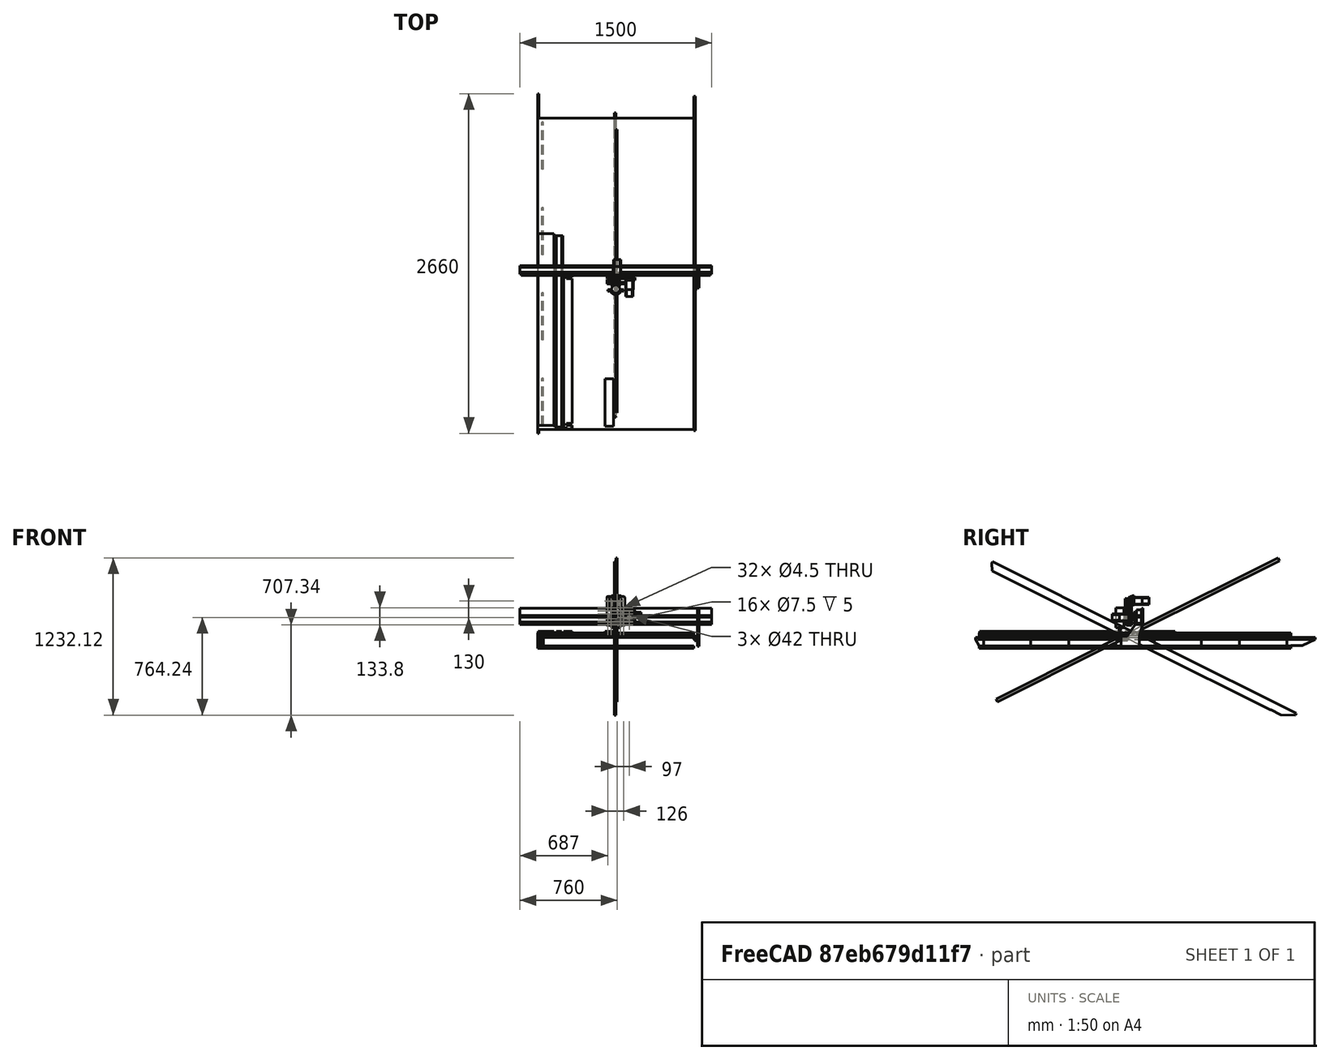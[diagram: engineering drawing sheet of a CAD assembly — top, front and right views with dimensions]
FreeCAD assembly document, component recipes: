
FREECAD ASSEMBLY — COMPONENT RECIPES ("humphrey2")

This assembly document has 11 components, labeled P0..P10 below (a component is one placed body or linked part). 10 of them carry a construction recipe — the FreeCAD feature program that regenerates the part from scratch, quoted from this document or its linked companion documents; the rest are supplied as boundary geometry only. No exploded tour is included for this assembly.
COMPONENT P0 — recipe-attached ("Core wall - outer", modeled in this document).
Construction recipe (the document's own serialized feature program — sketch geometry with constraints, then the solid features built on it; lengths are millimeters unless a unit is written):

FEATURE [Sketcher::SketchObject] Sketch006
  FullyConstrained = true
  MapMode = 5
  Placement = pos=(0,0,0) rot=(0.57735,0.57735,0.57735;2.0944rad)
  Support = -> [YZ_Plane004]
  expr: Constraints[18] = -dd.ddCore_heigth + 3
  expr: Constraints[20] = -dd.ddCore_heigth
  expr: Constraints[21] = dd.ddBed_size_Y / -2
  expr: Constraints[22] = dd.ddBed_size_Y / 2
  expr: Constraints[23] = dd.ddY_rail_length + 40
  expr: Constraints[8] = -dd.ddRail_width
  sketch-geometry (8):
    g0: LineSegment StartX=-1249.44 StartY=-15 StartZ=0 EndX=-1220 EndY=-66 EndZ=0
    g1: LineSegment StartX=1307.62 StartY=-63 StartZ=0 EndX=1410.56 EndY=-15 EndZ=0
    g2: LineSegment StartX=1410.56 StartY=-15 StartZ=0 EndX=1410.56 EndY=0 EndZ=0
    g3: LineSegment StartX=1410.56 StartY=0 StartZ=0 EndX=-1249.44 EndY=0 EndZ=0
    g4: LineSegment StartX=-1249.44 StartY=0 StartZ=0 EndX=-1249.44 EndY=-15 EndZ=0
    g5: LineSegment StartX=-1220 StartY=-66 StartZ=0 EndX=1220 EndY=-66 EndZ=0
    g6: LineSegment StartX=1220 StartY=-66 StartZ=0 EndX=1220 EndY=-63 EndZ=0
    g7: LineSegment StartX=1220 StartY=-63 StartZ=0 EndX=1307.62 EndY=-63 EndZ=0
  constraints (25):
    c: Coincident(g1,g2)
    c: Vertical(g2)
    c: Horizontal(g3)
    c: Coincident(g3,g4)
    c: Coincident(g4,g0)
    c: Vertical(g4)
    c: PointOnObject(g3,g-1)
    c: Angle(g0,g-1) = 1.0472
    c: DistanceY(g-1,g0) = -15
    c: Angle(g-1,g1) = 0.436332
    c: Coincident(g3,g2)
    c: Coincident(g0,g5)
    c: Coincident(g5,g6)
    c: Coincident(g6,g7)
    c: Horizontal(g7)
    c: Coincident(g7,g1)
    c: Horizontal(g5)
    c: Vertical(g6)
    c: DistanceY(g-1,g6) = -63
    c: Horizontal(g1,g0)
    c: DistanceY(g-1,g5) = -66
    c: DistanceX(g-2,g0) = -1220
    c: DistanceX(g-2,g5) = 1220
    c: Distance(g3) = 2660
    c: DistanceX(g-2,g3) = -1249.44  'frontpos'
FEATURE [PartDesign::Pad] Pad006
  Direction = (1,-2e-16,3e-16)
  Length = 11.6
  Length2 = 10
  Placement = pos=(0,0,0) rot=(0.57735,0.57735,0.57735;2.0944rad)
  Profile = -> Sketch006
  ReferenceAxis = -> Sketch006 [N_Axis]
  Reversed = true
  Type = 0
  expr: Length = dd.ddPhenolic_thickness
FEATURE [PartDesign::Body] Body004  label="Core wall - outer"
  Group = -> [Sketch006,Pad006]
  Origin = -> Origin004
  Placement = pos=(612,0,-37) rot=(0,0,1;0rad)
  Tip = -> Pad006
  expr: .Placement.Base.x = dd.ddBed_size_X / 2 + dd.ddCore_to_plywood_edge_dist
  expr: .Placement.Base.z = -dd.ddMDF_thickness - dd.ddPlywood_thickness
COMPONENT P1 — recipe-attached ("Cross wall - half", modeled in this document).
Construction recipe (the document's own serialized feature program — sketch geometry with constraints, then the solid features built on it; lengths are millimeters unless a unit is written):

FEATURE [Sketcher::SketchObject] Sketch008
  FullyConstrained = false
  MapMode = 5
  Placement = pos=(0,0,0) rot=(1,0,0;1.5708rad)
  Support = -> [XZ_Plane005]
  expr: Constraints[19] = -dd.ddCore_heigth
  sketch-geometry (12):
    g0: LineSegment StartX=0 StartY=0 StartZ=0 EndX=0 EndY=-66 EndZ=0
    g1: LineSegment StartX=0 StartY=-66 StartZ=0 EndX=566.008 EndY=-66 EndZ=0
    g2: LineSegment StartX=566.008 StartY=-66 StartZ=0 EndX=566.008 EndY=-21.8566 EndZ=0
    g3: LineSegment StartX=580.848 StartY=-21.8566 StartZ=0 EndX=580.848 EndY=-66 EndZ=0
    g4: LineSegment StartX=580.848 StartY=-66 StartZ=0 EndX=599.786 EndY=-66 EndZ=0
    g5: LineSegment StartX=599.786 StartY=-66 StartZ=0 EndX=599.786 EndY=-52.1636 EndZ=0
    g6: LineSegment StartX=599.786 StartY=-52.1636 StartZ=0 EndX=611.538 EndY=-52.1636 EndZ=0
    g7: LineSegment StartX=611.538 StartY=-52.1636 StartZ=0 EndX=611.538 EndY=-27.1139 EndZ=0
    g8: LineSegment StartX=611.538 StartY=-27.1139 StartZ=0 EndX=599.786 EndY=-27.1139 EndZ=0
    g9: LineSegment StartX=599.786 StartY=-27.1139 StartZ=0 EndX=599.786 EndY=0 EndZ=0
    g10: LineSegment StartX=599.786 StartY=0 StartZ=0 EndX=0 EndY=0 EndZ=0
    g11: LineSegment StartX=566.008 StartY=-21.8566 StartZ=0 EndX=580.848 EndY=-21.8566 EndZ=0
  constraints (28):
    c: PointOnObject(g0,g-2)
    c: Coincident(g0,g1)
    c: Horizontal(g1)
    c: Coincident(g1,g2)
    c: Vertical(g2)
    c: Vertical(g3)
    c: Coincident(g3,g4)
    c: Horizontal(g4)
    c: Coincident(g4,g5)
    c: Vertical(g5)
    c: Coincident(g5,g6)
    c: Coincident(g6,g7)
    c: Coincident(g7,g8)
    c: Coincident(g8,g9)
    c: Vertical(g9)
    c: Coincident(g9,g10)
    c: Coincident(g10,g0)
    c: Horizontal(g10)
    c: Coincident(g0,g-1)
    c: DistanceY(g-1,g0) = -66
    c: Horizontal(g8)
    c: Vertical(g7)
    c: Horizontal(g6)
    c: Vertical(g5,g8)
    c: Coincident(g11,g3)
    c: Coincident(g11,g2)
    c: Horizontal(g11)
    c: Horizontal(g1,g3)
FEATURE [PartDesign::Pad] Pad007
  Direction = (0,-1,-2e-16)
  Length = 11.6
  Length2 = 10
  Midplane = true
  Placement = pos=(0,0,0) rot=(1,0,0;1.5708rad)
  Profile = -> Sketch008
  ReferenceAxis = -> Sketch008 [N_Axis]
  Type = 0
  expr: Length = dd.ddPhenolic_thickness
FEATURE [PartDesign::Body] Body005  label="Cross wall - half"
  Group = -> [Sketch008,Pad007]
  Origin = -> Origin005
  Placement = pos=(0,0,-37) rot=(0,0,1;0rad)
  Tip = -> Pad007
  expr: .Placement.Base.z = -dd.ddMDF_thickness - dd.ddPlywood_thickness
COMPONENT P2 — recipe-attached ("Inner cross wall piece", modeled in this document).
Construction recipe (the document's own serialized feature program — sketch geometry with constraints, then the solid features built on it; lengths are millimeters unless a unit is written):

FEATURE [Sketcher::SketchObject] Sketch011
  FullyConstrained = true
  MapMode = 5
  Placement = pos=(0,0,0) rot=(0.57735,0.57735,0.57735;2.0944rad)
  Support = -> [YZ_Plane009]
  expr: Constraints[8] = -dd.ddCore_heigth
  expr: Constraints[9] = <<Cross walls>>.IntervalY[1] + dd.ddPhenolic_thickness * 3
  sketch-geometry (4):
    g0: LineSegment StartX=-184.543 StartY=0 StartZ=0 EndX=184.543 EndY=0 EndZ=0
    g1: LineSegment StartX=184.543 StartY=0 StartZ=0 EndX=184.543 EndY=-66 EndZ=0
    g2: LineSegment StartX=184.543 StartY=-66 StartZ=0 EndX=-184.543 EndY=-66 EndZ=0
    g3: LineSegment StartX=-184.543 StartY=-66 StartZ=0 EndX=-184.543 EndY=0 EndZ=0
  constraints (11):
    c: Coincident(g0,g1)
    c: Coincident(g1,g2)
    c: Coincident(g2,g3)
    c: Coincident(g3,g0)
    c: Horizontal(g0)
    c: Vertical(g1)
    c: Vertical(g3)
    c: PointOnObject(g0,g-1)
    c: DistanceY(g-1,g1) = -66
    c: Distance(g0) = 369.086
    c: Symmetric(g2,g1,g-2)
FEATURE [PartDesign::Pad] Pad010
  Direction = (1,-2e-16,3e-16)
  Length = 11.6
  Length2 = 10
  Placement = pos=(0,0,0) rot=(0.57735,0.57735,0.57735;2.0944rad)
  Profile = -> Sketch011
  ReferenceAxis = -> Sketch011 [N_Axis]
  Type = 0
  expr: Length = dd.ddPhenolic_thickness
FEATURE [PartDesign::Body] Body008  label="Inner cross wall piece"
  Group = -> [Sketch011,Pad010]
  Origin = -> Origin009
  Placement = pos=(567,0,-37) rot=(0,0,1;0rad)
  Tip = -> Pad010
  expr: .Placement.Base.x = dd.ddBed_size_X / 2 - dd.ddCore_wall_spacing + dd.ddCore_to_plywood_edge_dist
  expr: .Placement.Base.z = -dd.ddMDF_thickness - dd.ddPlywood_thickness
COMPONENT P3 — recipe-attached ("Rack Y", modeled in this document).
Construction recipe (the document's own serialized feature program — sketch geometry with constraints, then the solid features built on it; lengths are millimeters unless a unit is written):

FEATURE [Sketcher::SketchObject] Sketch012
  FullyConstrained = false
  MapMode = 5
  Placement = pos=(0,0,0) rot=(0.57735,0.57735,0.57735;2.0944rad)
  Support = -> [YZ_Plane011]
  expr: Constraints[10] = dd.ddBed_size_Y + 15 * 2
  sketch-geometry (4):
    g0: LineSegment StartX=-1205.46 StartY=0 StartZ=0 EndX=1264.54 EndY=0 EndZ=0
    g1: LineSegment StartX=1264.54 StartY=0 StartZ=0 EndX=1264.54 EndY=25 EndZ=0
    g2: LineSegment StartX=1264.54 StartY=25 StartZ=0 EndX=-1205.46 EndY=25 EndZ=0
    g3: LineSegment StartX=-1205.46 StartY=25 StartZ=0 EndX=-1205.46 EndY=0 EndZ=0
  constraints (11):
    c: Coincident(g0,g1)
    c: Coincident(g1,g2)
    c: Coincident(g2,g3)
    c: Coincident(g3,g0)
    c: Horizontal(g0)
    c: Horizontal(g2)
    c: Vertical(g1)
    c: Vertical(g3)
    c: PointOnObject(g0,g-1)
    c: DistanceY(g-1,g2) = 25
    c: Distance(g2) = 2470
FEATURE [PartDesign::Pad] Pad011
  Direction = (1,-2e-16,3e-16)
  Length = 10
  Length2 = 10
  Placement = pos=(0,0,0) rot=(0.57735,0.57735,0.57735;2.0944rad)
  Profile = -> Sketch012
  ReferenceAxis = -> Sketch012 [N_Axis]
  Type = 0
FEATURE [PartDesign::Body] Body009  label="Rack Y"
  Group = -> [Sketch012,Pad011]
  Origin = -> Origin011
  Placement = pos=(612,0,-94) rot=(0,0,1;0rad)
  Tip = -> Pad011
  expr: .Placement.Base.x = <<Core wall - outer>>.Placement.Base[0]
COMPONENT P4 — recipe-attached ("Rail Y", modeled in this document).
Construction recipe (the document's own serialized feature program — sketch geometry with constraints, then the solid features built on it; lengths are millimeters unless a unit is written):

FEATURE [Sketcher::SketchObject] Sketch013
  FullyConstrained = true
  MapMode = 5
  Placement = pos=(0,0,0) rot=(1,0,0;1.5708rad)
  Support = -> [XZ_Plane012]
  expr: Constraints[7] = dd.ddRail_heigth
  expr: Constraints[8] = dd.ddRail_width
  sketch-geometry (4):
    g0: LineSegment StartX=0 StartY=7.5 StartZ=0 EndX=13 EndY=7.5 EndZ=0
    g1: LineSegment StartX=13 StartY=7.5 StartZ=0 EndX=13 EndY=-7.5 EndZ=0
    g2: LineSegment StartX=13 StartY=-7.5 StartZ=0 EndX=0 EndY=-7.5 EndZ=0
    g3: LineSegment StartX=0 StartY=-7.5 StartZ=0 EndX=0 EndY=7.5 EndZ=0
  constraints (11):
    c: Coincident(g0,g1)
    c: Coincident(g1,g2)
    c: Coincident(g2,g3)
    c: Coincident(g3,g0)
    c: Horizontal(g0)
    c: Horizontal(g2)
    c: Vertical(g3)
    c: Distance(g2) = 13
    c: Distance(g1) = 15
    c: PointOnObject(g0,g-2)
    c: Symmetric(g0,g1,g-1)
FEATURE [PartDesign::Pad] Pad012
  Direction = (0,-1,-2e-16)
  Length = 2620
  Length2 = 10
  Placement = pos=(0,0,0) rot=(1,0,0;1.5708rad)
  Profile = -> Sketch013
  ReferenceAxis = -> Sketch013 [N_Axis]
  Reversed = true
  Type = 0
  expr: Length = dd.ddY_rail_length
FEATURE [PartDesign::Body] Body010  label="Rail Y"
  Group = -> [Sketch013,Pad012]
  Origin = -> Origin012
  Placement = pos=(612,-1229.44,-44.5) rot=(0,0,1;0rad)
  Tip = -> Pad012
  expr: .Placement.Base.x = dd.ddBed_size_X / 2 + dd.ddCore_to_plywood_edge_dist
  expr: .Placement.Base.y = Sketch006.Constraints.frontpos + 20mm
  expr: .Placement.Base.z = -dd.ddMDF_thickness - dd.ddPlywood_thickness - dd.ddRail_width / 2
COMPONENT P5 — recipe-attached ("Gearbox and nema23 motor", modeled in this document).
Construction recipe (the document's own serialized feature program — sketch geometry with constraints, then the solid features built on it; lengths are millimeters unless a unit is written):

FEATURE [Sketcher::SketchObject] Sketch025
  FullyConstrained = true
  MapMode = 5
  Placement = pos=(0,0,0) rot=(1,0,0;1.5708rad)
  Support = -> [XZ_Plane025]
  expr: Constraints[10] = dd.ddGearbox_width
  expr: Constraints[11] = dd.ddGearbox_width
  sketch-geometry (5):
    g0: LineSegment StartX=-30 StartY=-30 StartZ=0 EndX=-30 EndY=30 EndZ=0
    g1: LineSegment StartX=-30 StartY=30 StartZ=0 EndX=30 EndY=30 EndZ=0
    g2: LineSegment StartX=30 StartY=30 StartZ=0 EndX=30 EndY=-30 EndZ=0
    g3: LineSegment StartX=30 StartY=-30 StartZ=0 EndX=-30 EndY=-30 EndZ=0
    g4: GeomPoint X=0 Y=0 Z=0
  constraints (12):
    c: Coincident(g0,g1)
    c: Coincident(g1,g2)
    c: Coincident(g2,g3)
    c: Coincident(g3,g0)
    c: Horizontal(g1)
    c: Horizontal(g3)
    c: Vertical(g0)
    c: Vertical(g2)
    c: Symmetric(g1,g0,g4)
    c: Coincident(g4,g-1)
    c: Distance(g2) = 60
    c: Distance(g1) = 60
FEATURE [PartDesign::Pad] Pad022
  Direction = (0,-1,-2e-16)
  Length = 73
  Length2 = 10
  Placement = pos=(0,0,0) rot=(1,0,0;1.5708rad)
  Profile = -> Sketch025
  ReferenceAxis = -> Sketch025 [N_Axis]
  Type = 0
FEATURE [Sketcher::SketchObject] Sketch026
  FullyConstrained = true
  MapMode = 5
  Placement = pos=(0,-73,1e-16) rot=(1,0,0;1.5708rad)
  Support = -> [Pad022]
  sketch-geometry (5):
    g0: LineSegment StartX=-28.5 StartY=-28.5 StartZ=0 EndX=-28.5 EndY=28.5 EndZ=0
    g1: LineSegment StartX=-28.5 StartY=28.5 StartZ=0 EndX=28.5 EndY=28.5 EndZ=0
    g2: LineSegment StartX=28.5 StartY=28.5 StartZ=0 EndX=28.5 EndY=-28.5 EndZ=0
    g3: LineSegment StartX=28.5 StartY=-28.5 StartZ=0 EndX=-28.5 EndY=-28.5 EndZ=0
    g4: GeomPoint X=0 Y=0 Z=0
  constraints (12):
    c: Coincident(g0,g1)
    c: Coincident(g1,g2)
    c: Coincident(g2,g3)
    c: Coincident(g3,g0)
    c: Horizontal(g1)
    c: Horizontal(g3)
    c: Vertical(g0)
    c: Vertical(g2)
    c: Symmetric(g1,g0,g4)
    c: Coincident(g4,g-1)
    c: Distance(g2) = 57
    c: Equal(g1,g2)
FEATURE [PartDesign::Pad] Pad023
  BaseFeature = -> Pad022
  Direction = (0,-1,-2e-16)
  Length = 54
  Length2 = 10
  Placement = pos=(0,0,0) rot=(1,0,0;1.5708rad)
  Profile = -> Sketch026
  ReferenceAxis = -> Sketch026 [N_Axis]
  Type = 0
FEATURE [PartDesign::Chamfer] Chamfer
  Angle = 45
  Base = -> Pad023 [Edge18,Edge17,Edge22,Edge20]
  BaseFeature = -> Pad023
  ChamferType = 0
  FlipDirection = false
  Placement = pos=(0,0,0) rot=(1,0,0;1.5708rad)
  Size = 6
  Size2 = 1
  SupportTransform = false
  UseAllEdges = false
FEATURE [PartDesign::Chamfer] Chamfer001
  Angle = 45
  Base = -> Chamfer [Edge34,Edge29,Edge30,Edge32]
  BaseFeature = -> Chamfer
  ChamferType = 0
  FlipDirection = false
  Placement = pos=(0,0,0) rot=(1,0,0;1.5708rad)
  Size = 4
  Size2 = 1
  SupportTransform = false
  UseAllEdges = false
FEATURE [PartDesign::Body] Body020  label="Gearbox and nema23 motor"
  Group = -> [Sketch025,Pad022,Sketch026,Pad023,Chamfer,Chamfer001]
  Origin = -> Origin025
  Tip = -> Chamfer001
COMPONENT P6 — recipe-attached ("Pinion", a linked part whose construction recipe lives in a companion FreeCAD document of the same project; that document's serialized recipe follows).
Construction recipe (the companion document, serialized — sketch geometry with constraints, then the solid features built on it; lengths are millimeters unless a unit is written):

FCSTD DOCUMENT  (FreeCAD 0.20R29177 (Git))
Label: cnc-friendy-rack-and-pinion-for-humphrey2
License: All rights reserved
LicenseURL: http://en.wikipedia.org/wiki/All_rights_reserved
objects: Part::FeaturePython×50, Part::Mirroring×7, PartDesign::Body×6, Part::Cut×6, Part::Cylinder×6, Sketcher::SketchObject×5, PartDesign::FeatureBase×4, App::DocumentObjectGroup×3, Part::Offset×2, PartDesign::Pad×2, PartDesign::Fillet×2, Part::MultiFuse×2, Spreadsheet::Sheet×1, Part::Feature×1, Part::Box×1, PartDesign::ShapeBinder×1, Part::Loft×1, Part::MultiCommon×1, Part::Compound×1, Part::RuledSurface×1, +2 more types
note: 105 computed .brp shape members not serialized (recipe doc carries the construction recipe); baked Part::Feature solids carry a one-line shape summary decoded from their .brp

FEATURE [Spreadsheet::Sheet] Spreadsheet
  cells = A1=Main adjustements; A2=Number of pinion teeth; B2(pinion_tooth_count)=20; A3=Pinion tooth width; B3(pinion_tooth_width)=3.3; A4=Pinion tooth heigth; B4(pinion_tooth_heigth)=8; A5=Rack tooth spacing; B5(rack_tooth_spacing)=5.75; A6=Rack width; B6(rack_width)=20; A7=Rack thickness; B7(rack_thickness)=8; A8=Rack length; B8(rack_length)=205; A10=Advanced adjustments; A11=Motor shaft diameter; B11(pinion_motor_shaft_diameter)=7.2; A12=Motor shaft flat depth; B12(pinion_motor_shaft_flat_depth)=0.5; A13=Motor shaft flat corner dogbone diameter; B13(pinion_motor_shaft_flat_dogbone_diameter)=3.1; A14=Motorshaft hole dogbone angle; B14(pinion_dogbone_angle)=75; A15=Rack tooth fillet ratio; B15(rack_tooth_fillet_ratio)=0.1; A16=Pinion valley to rack tooth tip clearance; B16(pinion_side_clearance)=0.12; A17=Pinion to rack heigth clearance; B17(pinion_heigth_clearance)=0.5; A18=Pinion dust relief trim distance; B18(dust_relief)=0.5; A19=Pinion dust relief fillet ratio; B19(dust_relief_fillet_ratio)=0.1; A20=Pinion stock thickness; B20(pinion_stock_thick)=25; A21=Pinion ring diameter; B21(pinion_ring_diameter)=39; A22=Pinion set screw hole diameter; B22(pinion_set_screw_hole_diameter)=4.3; A23=Pinion set screw count; B23(pinion_set_screw_count)=3; A25=Inputs not to be changed:; A26=Master cycloid circumference; B26(master_cycloid_circumference)=100; A29=Deducted values (not to be changed):; A30=Pinion circumference; B30(pinion_circumference)==pinion_tooth_count * rack_tooth_spacing; A31=Pinion tooth gap size; B31(pinion_tooth_gap_size)==rack_tooth_spacing - pinion_tooth_width
FEATURE [Part::Feature] Part__Feature  label="Master-cycloid"
  shape: bbox 100 x 100 x 81.83 mm, 7 faces (baked)
FEATURE [Part::FeaturePython] Clone  label="Master-cycloid-scaled-and-moved"  # Draft clone (typed FeaturePython)
  AttacherType = Attacher::AttachEngine3D
  Fuse = false
  Objects = -> [Part__Feature]
  Placement = pos=(-2.875,0,0) rot=(0,0,1;0rad)
  Scale = (1.15,1.15,1.15)
  expr: .Placement.Base.x = Spreadsheet.rack_tooth_spacing / 2 * -1
  expr: .Scale.x = Spreadsheet.pinion_circumference / Spreadsheet.master_cycloid_circumference
  expr: .Scale.y = Spreadsheet.pinion_circumference / Spreadsheet.master_cycloid_circumference
  expr: .Scale.z = Spreadsheet.pinion_circumference / Spreadsheet.master_cycloid_circumference
FEATURE [Part::Offset] Offset
  Fill = false
  Intersection = false
  Join = 0
  Mode = 0
  SelfIntersection = false
  Source = -> Clone
  Value = 1.65
  expr: Value = Spreadsheet.pinion_tooth_width / 2
FEATURE [Part::Mirroring] Part__Mirroring  label="Offset (Mirror #1)"
  Base = (0,0,0)
  Normal = (1,0,0)
  Source = -> Offset
FEATURE [Sketcher::SketchObject] Sketch
  FullyConstrained = true
  MapMode = 5
  Placement = pos=(0,0,0) rot=(1,0,0;1.5708rad)
  Support = -> [XZ_Plane]
  expr: Constraints[10] = Spreadsheet.rack_tooth_spacing / -2
  expr: Constraints[11] = Spreadsheet.rack_width + Spreadsheet.pinion_tooth_width / 2
  expr: Constraints[8] = Spreadsheet.rack_tooth_spacing
  expr: Constraints[9] = Spreadsheet.rack_width + Spreadsheet.rack_tooth_spacing * 3
  sketch-geometry (4):
    g0: LineSegment StartX=-2.875 StartY=15.6 StartZ=0 EndX=2.875 EndY=15.6 EndZ=0
    g1: LineSegment StartX=2.875 StartY=15.6 StartZ=0 EndX=2.875 EndY=-21.65 EndZ=0
    g2: LineSegment StartX=2.875 StartY=-21.65 StartZ=0 EndX=-2.875 EndY=-21.65 EndZ=0
    g3: LineSegment StartX=-2.875 StartY=-21.65 StartZ=0 EndX=-2.875 EndY=15.6 EndZ=0
  constraints (12):
    c: Coincident(g0,g1)
    c: Coincident(g1,g2)
    c: Coincident(g2,g3)
    c: Coincident(g3,g0)
    c: Horizontal(g0)
    c: Horizontal(g2)
    c: Vertical(g1)
    c: Vertical(g3)
    c: DistanceX(g2,g2) = 5.75
    c: DistanceY(g1,g1) = 37.25
    c: DistanceX(g1,g-1) = -2.875
    c: DistanceY(g1,g-1) = 21.65
FEATURE [PartDesign::Pad] Pad
  AllowMultiFace = false
  Direction = (1,1,1)
  Length = 8
  Length2 = 100
  Placement = pos=(0,0,0) rot=(1,0,0;1.5708rad)
  Profile = -> Sketch
  Type = 0
  expr: Length = Spreadsheet.rack_thickness
FEATURE [PartDesign::Body] Body
  Group = -> [Sketch,Pad]
  Origin = -> Origin
  Tip = -> Pad
FEATURE [Part::Cut] Cut
  Base = -> Pad
  Tool = -> Offset
FEATURE [Part::Cut] Cut001
  Base = -> Cut
  Tool = -> Part__Mirroring
FEATURE [PartDesign::FeatureBase] BaseFeature
  BaseFeature = -> Cut001
FEATURE [PartDesign::Fillet] Fillet
  Base = -> BaseFeature [Edge21]
  BaseFeature = -> BaseFeature
  Radius = 0.575
  SupportTransform = false
  UseAllEdges = false
  expr: Radius = Spreadsheet.rack_tooth_spacing * Spreadsheet.rack_tooth_fillet_ratio
FEATURE [PartDesign::Body] Body001
  BaseFeature = -> Cut001
  Group = -> [BaseFeature,Fillet]
  Origin = -> Origin001
  Placement = pos=(0,0,-6.3662) rot=(0,0,1;0rad)
  Tip = -> Fillet
  expr: .Placement.Base.x = 0
FEATURE [Part::FeaturePython] Array  label="Rack"  # Draft array (typed FeaturePython)
  Angle = 360
  ArrayType = 0
  Axis = (0,0,1)
  Base = -> Fillet
  Center = (0,0,0)
  Fuse = true
  IntervalAxis = (0,0,0)
  IntervalX = (5.75,0,0)
  IntervalY = (0,1,0)
  IntervalZ = (0,0,1)
  NumberPolar = 1
  NumberX = 36
  NumberY = 1
  NumberZ = 1
  Placement = pos=(-5.75,0,-18.3028) rot=(0,0,1;0rad)
  expr: .IntervalX.x = Spreadsheet.rack_tooth_spacing
  expr: .Placement.Base.x = Spreadsheet.rack_tooth_spacing * -1
  expr: .Placement.Base.z = Spreadsheet.pinion_circumference / pi / -2
  expr: NumberX = Spreadsheet.rack_length / Spreadsheet.rack_tooth_spacing
FEATURE [Part::Box] Box  label="Cube"
  AttacherType = Attacher::AttachEngine3D
  Height = 250
  Length = 11.5
  Placement = pos=(0,-8,-135) rot=(0,0,1;0rad)
  Width = 8
  expr: .Placement.Base.y = Spreadsheet.rack_thickness * -1
  expr: .Placement.Base.z = (Spreadsheet.rack_width + Spreadsheet.pinion_circumference) * -1
  expr: Height = Spreadsheet.rack_width + Spreadsheet.pinion_circumference * 2
  expr: Length = Spreadsheet.rack_tooth_spacing * 2
  expr: Width = Spreadsheet.rack_thickness
FEATURE [Part::Cut] Cut002  label="Halftooth for sampling"
  Base = -> Fillet
  Placement = pos=(0,0,-18.3028) rot=(0,0,1;0rad)
  Tool = -> Box
  expr: .Placement.Base.z = Spreadsheet.pinion_circumference / pi / -2
FEATURE [PartDesign::ShapeBinder] ShapeBinder
  Placement = pos=(0,0,-18.3028) rot=(0,0,1;0rad)
  Support = -> [Cut002]
  TraceSupport = false
FEATURE [Sketcher::SketchObject] Sketch001
  ExternalGeometry = -> [ShapeBinder]
  FullyConstrained = true
  MapMode = 5
  Placement = pos=(0,0,0) rot=(0.57735,0.57735,0.57735;2.0944rad)
  Support = -> [YZ_Plane005]
  expr: Constraints[3] = Spreadsheet.rack_tooth_spacing * Spreadsheet.rack_tooth_fillet_ratio
  sketch-geometry (1):
    g0: LineSegment StartX=-8 StartY=-15.4427 StartZ=0 EndX=3.6e-15 EndY=-15.4427 EndZ=0
  constraints (4):
    c: Horizontal(g0)
    c: DistanceX(g0,g-3) = 0
    c: DistanceX(g0,g-3) = 0
    c: DistanceY(g0,g-3) = 0.575
FEATURE [PartDesign::Body] Body005  label="Body for extrating tooth tip center line"
  Group = -> [Sketch001,ShapeBinder]
  Origin = -> Origin005
FEATURE [Part::FeaturePython] Array001  label="Center line"  # Draft array (typed FeaturePython)
  Angle = 360
  ArrayType = 0
  Axis = (0,0,1)
  Base = -> Sketch001
  Center = (0,0,0)
  Fuse = false
  IntervalAxis = (0,0,0)
  IntervalX = (1,0,0)
  IntervalY = (0,1,0)
  IntervalZ = (0,0,1)
  NumberPolar = 1
  NumberX = 1
  NumberY = 1
  NumberZ = 1
FEATURE [Part::FeaturePython] Array002  label="Rigth1-move"  # Draft array (typed FeaturePython)
  Angle = 360
  ArrayType = 0
  Axis = (0,0,1)
  Base = -> Sketch001
  Center = (0,0,0)
  Fuse = false
  IntervalAxis = (0,0,0)
  IntervalX = (1,0,0)
  IntervalY = (0,1,0)
  IntervalZ = (0,0,1)
  NumberPolar = 1
  NumberX = 1
  NumberY = 1
  NumberZ = 1
  Placement = pos=(2.55556,0,0) rot=(0,0,1;0rad)
  expr: .Placement.Base.x = Spreadsheet.pinion_circumference / (360 / 8)
FEATURE [Part::FeaturePython] Array003  label="Rigth1-rotate"  # Draft array (typed FeaturePython)
  Angle = 0
  ArrayType = 0
  Axis = (0,0,1)
  Base = -> Array002
  Center = (0,0,0)
  Fuse = false
  IntervalAxis = (0,0,0)
  IntervalX = (1,0,0)
  IntervalY = (0,1,0)
  IntervalZ = (0,0,1)
  NumberPolar = 1
  NumberX = 1
  NumberY = 1
  NumberZ = 1
  Placement = pos=(0,0,0) rot=(0,1,0;0.139626rad)
  expr: .Placement.Base.x = 0
FEATURE [Part::FeaturePython] Array004  label="Right2-move"  # Draft array (typed FeaturePython)
  Angle = 360
  ArrayType = 0
  Axis = (0,0,1)
  Base = -> Sketch001
  Center = (0,0,0)
  Fuse = false
  IntervalAxis = (0,0,0)
  IntervalX = (1,0,0)
  IntervalY = (0,1,0)
  IntervalZ = (0,0,1)
  NumberPolar = 1
  NumberX = 1
  NumberY = 1
  NumberZ = 1
  Placement = pos=(5.11111,0,0) rot=(0,0,1;0rad)
  expr: .Placement.Base.x = Spreadsheet.pinion_circumference / (360 / 16)
FEATURE [Part::FeaturePython] Array005  label="Right2-rotate"  # Draft array (typed FeaturePython)
  Angle = 0
  ArrayType = 0
  Axis = (0,0,1)
  Base = -> Array004
  Center = (0,0,0)
  Fuse = false
  IntervalAxis = (0,0,0)
  IntervalX = (1,0,0)
  IntervalY = (0,1,0)
  IntervalZ = (0,0,1)
  NumberPolar = 1
  NumberX = 1
  NumberY = 1
  NumberZ = 1
  Placement = pos=(0,0,0) rot=(0,1,0;0.279253rad)
FEATURE [Part::FeaturePython] Array006  label="Right3-move"  # Draft array (typed FeaturePython)
  Angle = 360
  ArrayType = 0
  Axis = (0,0,1)
  Base = -> Sketch001
  Center = (0,0,0)
  Fuse = false
  IntervalAxis = (0,0,0)
  IntervalX = (1,0,0)
  IntervalY = (0,1,0)
  IntervalZ = (0,0,1)
  NumberPolar = 1
  NumberX = 1
  NumberY = 1
  NumberZ = 1
  Placement = pos=(7.66667,0,0) rot=(0,0,1;0rad)
  expr: .Placement.Base.x = Spreadsheet.pinion_circumference / (360 / 24)
FEATURE [Part::FeaturePython] Array007  label="Right3-rotate"  # Draft array (typed FeaturePython)
  Angle = 360
  ArrayType = 0
  Axis = (0,0,1)
  Base = -> Array006
  Center = (0,0,0)
  Fuse = false
  IntervalAxis = (0,0,0)
  IntervalX = (1,0,0)
  IntervalY = (0,1,0)
  IntervalZ = (0,0,1)
  NumberPolar = 1
  NumberX = 1
  NumberY = 1
  NumberZ = 1
  Placement = pos=(0,0,0) rot=(0,1,0;0.418879rad)
FEATURE [Part::FeaturePython] Array008  label="Right4-move "  # Draft array (typed FeaturePython)
  Angle = 360
  ArrayType = 0
  Axis = (0,0,1)
  Base = -> Sketch001
  Center = (0,0,0)
  Fuse = false
  IntervalAxis = (0,0,0)
  IntervalX = (1,0,0)
  IntervalY = (0,1,0)
  IntervalZ = (0,0,1)
  NumberPolar = 1
  NumberX = 1
  NumberY = 1
  NumberZ = 1
  Placement = pos=(10.2222,0,0) rot=(0,0,1;0rad)
  expr: .Placement.Base.x = Spreadsheet.pinion_circumference / (360 / 32)
FEATURE [Part::FeaturePython] Array009  label="Right4-rotate"  # Draft array (typed FeaturePython)
  Angle = 360
  ArrayType = 0
  Axis = (0,0,1)
  Base = -> Array008
  Center = (0,0,0)
  Fuse = false
  IntervalAxis = (0,0,0)
  IntervalX = (1,0,0)
  IntervalY = (0,1,0)
  IntervalZ = (0,0,1)
  NumberPolar = 1
  NumberX = 1
  NumberY = 1
  NumberZ = 1
  Placement = pos=(0,0,0) rot=(0,1,0;0.558505rad)
FEATURE [Part::FeaturePython] Array010  label="Right5-move"  # Draft array (typed FeaturePython)
  Angle = 360
  ArrayType = 0
  Axis = (0,0,1)
  Base = -> Sketch001
  Center = (0,0,0)
  Fuse = false
  IntervalAxis = (0,0,0)
  IntervalX = (1,0,0)
  IntervalY = (0,1,0)
  IntervalZ = (0,0,1)
  NumberPolar = 1
  NumberX = 1
  NumberY = 1
  NumberZ = 1
  Placement = pos=(12.7778,0,0) rot=(0,0,1;0rad)
  expr: .Placement.Base.x = Spreadsheet.pinion_circumference / (360 / 40)
FEATURE [Part::FeaturePython] Array011  label="Right5-rotate"  # Draft array (typed FeaturePython)
  Angle = 360
  ArrayType = 0
  Axis = (0,0,1)
  Base = -> Array010
  Center = (0,0,0)
  Fuse = false
  IntervalAxis = (0,0,0)
  IntervalX = (1,0,0)
  IntervalY = (0,1,0)
  IntervalZ = (0,0,1)
  NumberPolar = 1
  NumberX = 1
  NumberY = 1
  NumberZ = 1
  Placement = pos=(0,0,0) rot=(0,1,0;0.698132rad)
FEATURE [Part::FeaturePython] Array012  label="Right6-move"  # Draft array (typed FeaturePython)
  Angle = 360
  ArrayType = 0
  Axis = (0,0,1)
  Base = -> Sketch001
  Center = (0,0,0)
  Fuse = false
  IntervalAxis = (0,0,0)
  IntervalX = (1,0,0)
  IntervalY = (0,1,0)
  IntervalZ = (0,0,1)
  NumberPolar = 1
  NumberX = 1
  NumberY = 1
  NumberZ = 1
  Placement = pos=(15.3333,0,0) rot=(0,1,0;0rad)
  expr: .Placement.Base.x = Spreadsheet.pinion_circumference / (360 / 48)
FEATURE [Part::FeaturePython] Array013  label="Right6-rotate"  # Draft array (typed FeaturePython)
  Angle = 360
  ArrayType = 0
  Axis = (0,0,1)
  Base = -> Array012
  Center = (0,0,0)
  Fuse = false
  IntervalAxis = (0,0,0)
  IntervalX = (1,0,0)
  IntervalY = (0,1,0)
  IntervalZ = (0,0,1)
  NumberPolar = 1
  NumberX = 1
  NumberY = 1
  NumberZ = 1
  Placement = pos=(0,0,0) rot=(0,1,0;0.837758rad)
FEATURE [Part::Mirroring] Part__Mirroring001  label="Rigth1-rotate (Mirror #2)"
  Base = (0,0,0)
  Normal = (1,0,0)
  Source = -> Array003
FEATURE [Part::Mirroring] Part__Mirroring002  label="Right2-rotate (Mirror #3)"
  Base = (0,0,0)
  Normal = (1,0,0)
  Source = -> Array005
FEATURE [Part::Mirroring] Part__Mirroring003  label="Right3-rotate (Mirror #4)"
  Base = (0,0,0)
  Normal = (1,0,0)
  Source = -> Array007
FEATURE [Part::Mirroring] Part__Mirroring004  label="Right4-rotate (Mirror #5)"
  Base = (0,0,0)
  Normal = (1,0,0)
  Source = -> Array009
FEATURE [Part::Mirroring] Part__Mirroring005  label="Right5-rotate (Mirror #6)"
  Base = (0,0,0)
  Normal = (1,0,0)
  Source = -> Array011
FEATURE [Part::Mirroring] Part__Mirroring006  label="Right6-rotate (Mirror #7)"
  Base = (0,0,0)
  Normal = (1,0,0)
  Source = -> Array013
FEATURE [Part::FeaturePython] Connect  # WARN: FeaturePython — macro-defined, semantics opaque (R4)
  Objects = -> [Array003]
  Tolerance = 0
FEATURE [Part::FeaturePython] Connect001  # WARN: FeaturePython — macro-defined, semantics opaque (R4)
  Objects = -> [Array005]
  Tolerance = 0
FEATURE [Part::FeaturePython] Connect002  # WARN: FeaturePython — macro-defined, semantics opaque (R4)
  Objects = -> [Array007]
  Tolerance = 0
FEATURE [Part::FeaturePython] Connect003  # WARN: FeaturePython — macro-defined, semantics opaque (R4)
  Objects = -> [Array009]
  Tolerance = 0
FEATURE [Part::FeaturePython] Connect004  # WARN: FeaturePython — macro-defined, semantics opaque (R4)
  Objects = -> [Array011]
  Tolerance = 0
FEATURE [Part::FeaturePython] Connect005  # WARN: FeaturePython — macro-defined, semantics opaque (R4)
  Objects = -> [Array013]
  Tolerance = 0
FEATURE [Part::FeaturePython] Connect006  # WARN: FeaturePython — macro-defined, semantics opaque (R4)
  Objects = -> [Part__Mirroring001]
  Tolerance = 0
FEATURE [Part::FeaturePython] Connect007  # WARN: FeaturePython — macro-defined, semantics opaque (R4)
  Objects = -> [Part__Mirroring002]
  Tolerance = 0
FEATURE [Part::FeaturePython] Connect008  # WARN: FeaturePython — macro-defined, semantics opaque (R4)
  Objects = -> [Part__Mirroring003]
  Tolerance = 0
FEATURE [Part::FeaturePython] Connect009  # WARN: FeaturePython — macro-defined, semantics opaque (R4)
  Objects = -> [Part__Mirroring004]
  Tolerance = 0
FEATURE [Part::FeaturePython] Connect010  # WARN: FeaturePython — macro-defined, semantics opaque (R4)
  Objects = -> [Part__Mirroring005]
  Tolerance = 0
FEATURE [Part::FeaturePython] Connect011  # WARN: FeaturePython — macro-defined, semantics opaque (R4)
  Objects = -> [Part__Mirroring006]
  Tolerance = 0
FEATURE [Part::Loft] Loft
  Closed = false
  MaxDegree = 2
  Ruled = false
  Sections = -> [Connect011,Connect010,Connect009,Connect008,Connect007,Connect006,Array001,Connect,Connect001,Connect002,Connect003,Connect004,Connect005]
  Solid = false
FEATURE [Part::Offset] Offset001  label="Inner pinion profile before trim"
  Fill = false
  Intersection = false
  Join = 0
  Mode = 0
  SelfIntersection = false
  Source = -> Loft
  Value = -0.695
  expr: Value = (Spreadsheet.rack_tooth_spacing * Spreadsheet.rack_tooth_fillet_ratio + Spreadsheet.pinion_side_clearance) * -1
FEATURE [Part::Cylinder] Cylinder  label="ToothCylinder"
  Angle = 360
  AttacherType = Attacher::AttachEngine3D
  FirstAngle = 0
  Height = 8
  Placement = pos=(0,0,-18.3028) rot=(1,0,0;1.5708rad)
  Radius = 1.65
  SecondAngle = 0
  expr: .Placement.Base.x = 0
  expr: .Placement.Base.z = Spreadsheet.pinion_circumference / pi / -2
  expr: Height = Spreadsheet.pinion_tooth_heigth
  expr: Radius = Spreadsheet.pinion_tooth_width / 2
FEATURE [Part::Cylinder] Cylinder001  label="TrimCylinder"
  Angle = 360
  AttacherType = Attacher::AttachEngine3D
  FirstAngle = 0
  Height = 8
  Placement = pos=(0,0,0) rot=(1,0,0;1.5708rad)
  Radius = 19.4528
  SecondAngle = 0
  expr: Height = Spreadsheet.pinion_tooth_heigth
  expr: Radius = (Spreadsheet.pinion_circumference / pi + Spreadsheet.pinion_tooth_width) / 2 - Spreadsheet.dust_relief
FEATURE [Part::MultiCommon] Common  label="Tooth before fillet"
  Shapes = -> [Cylinder,Cylinder001]
FEATURE [PartDesign::FeatureBase] BaseFeature002
  BaseFeature = -> Common
FEATURE [PartDesign::Fillet] Fillet002
  Base = -> BaseFeature002 [Edge6,Edge3]
  BaseFeature = -> BaseFeature002
  Radius = 0.33
  SupportTransform = false
  UseAllEdges = false
  expr: Radius = Spreadsheet.pinion_tooth_width * Spreadsheet.dust_relief_fillet_ratio
FEATURE [PartDesign::Body] Body006  label="Pinion tooth with dust relief"
  BaseFeature = -> Common
  Group = -> [BaseFeature002,Fillet002]
  Origin = -> Origin006
  Tip = -> Fillet002
FEATURE [Part::FeaturePython] Clone001  label="Left trim pinion"  # Draft clone (typed FeaturePython)
  AttacherType = Attacher::AttachEngine3D
  Fuse = false
  Objects = -> [Fillet002]
  Placement = pos=(0,0,0) rot=(0,1,0;0.15708rad)
  Scale = (1,1,1)
  expr: .Placement.Rotation.Angle = 360 / Spreadsheet.pinion_tooth_count / 2
FEATURE [Part::FeaturePython] Clone002  label="Rigth trim pinion"  # Draft clone (typed FeaturePython)
  AttacherType = Attacher::AttachEngine3D
  Fuse = false
  Objects = -> [Body006]
  Placement = pos=(0,0,0) rot=(0,-1,0;0.15708rad)
  Scale = (1,1,1)
  expr: .Placement.Rotation.Angle = 360 / Spreadsheet.pinion_tooth_count / 2
FEATURE [Part::Compound] Compound
  Links = -> [Clone001,Clone002]
FEATURE [Part::FeaturePython] Slice  # WARN: FeaturePython — macro-defined, semantics opaque (R4)
  Base = -> Offset001
  Mode = 1
  Tolerance = 0
  Tools = -> [Compound]
FEATURE [Part::FeaturePython] Slice_child0  label="Slice.0"  # WARN: FeaturePython — macro-defined, semantics opaque (R4)
  Base = -> Slice
  FilterType = 1
  Invert = false
  OverrideMaxVal = 0
  WindowFrom = 80
  WindowTo = 100
  items = 0
FEATURE [Part::FeaturePython] Slice_child1  label="Slice.1"  # WARN: FeaturePython — macro-defined, semantics opaque (R4)
  Base = -> Slice
  FilterType = 1
  Invert = false
  OverrideMaxVal = 0
  WindowFrom = 80
  WindowTo = 100
  items = 1
FEATURE [Part::FeaturePython] Slice_child2  label="Slice.2"  # WARN: FeaturePython — macro-defined, semantics opaque (R4)
  Base = -> Slice
  FilterType = 1
  Invert = false
  OverrideMaxVal = 0
  WindowFrom = 80
  WindowTo = 100
  items = 2
FEATURE [Part::FeaturePython] Slice_child3  label="Slice.3"  # WARN: FeaturePython — macro-defined, semantics opaque (R4)
  Base = -> Slice
  FilterType = 1
  Invert = false
  OverrideMaxVal = 0
  WindowFrom = 80
  WindowTo = 100
  items = 3
FEATURE [Part::FeaturePython] Slice_child4  label="Slice.4"  # WARN: FeaturePython — macro-defined, semantics opaque (R4)
  Base = -> Slice
  FilterType = 1
  Invert = false
  OverrideMaxVal = 0
  WindowFrom = 80
  WindowTo = 100
  items = 4
FEATURE [App::DocumentObjectGroup] GrExplode_Slice  label="Exploded Slice for inner skin"
  Group = -> [Slice_child0,Slice_child1,Slice_child2,Slice_child3,Slice_child4]
FEATURE [Part::FeaturePython] Clone003  label="Skin for line1"  # Draft clone (typed FeaturePython)
  AttacherType = Attacher::AttachEngine3D
  Fuse = false
  Objects = -> [Slice_child2]
  Scale = (1,1,1)
FEATURE [Part::FeaturePython] Clone004  label="Skin for line2"  # Draft clone (typed FeaturePython)
  AttacherType = Attacher::AttachEngine3D
  Fuse = false
  Objects = -> [Clone003]
  Placement = pos=(0,0,0) rot=(0,1,0;0.314159rad)
  Scale = (1,1,1)
  expr: .Placement.Rotation.Angle = 360 / Spreadsheet.pinion_tooth_count
FEATURE [Part::RuledSurface] Ruled_Surface
  Curve1 = -> Clone004 [Edge2]
  Curve2 = -> Slice_child2 [Edge4]
  Orientation = 0
FEATURE [Part::FeaturePython] Connect012  label="Inner profile and connection"  # WARN: FeaturePython — macro-defined, semantics opaque (R4)
  Objects = -> [Clone003,Ruled_Surface]
  Tolerance = 0
FEATURE [Part::FeaturePython] Array014  # Draft array (typed FeaturePython)
  Angle = 360
  ArrayType = 1
  Axis = (0,1,0)
  Base = -> Connect012
  Center = (0,0,0)
  Fuse = false
  IntervalAxis = (0,0,0)
  IntervalX = (1,0,0)
  IntervalY = (0,1,0)
  IntervalZ = (0,0,1)
  NumberPolar = 20
  NumberX = 1
  NumberY = 1
  NumberZ = 1
  expr: NumberPolar = Spreadsheet.pinion_tooth_count
FEATURE [Part::FeaturePython] Connect013  label="Connected inner skins"  # WARN: FeaturePython — macro-defined, semantics opaque (R4)
  Objects = -> [Array014]
  Tolerance = 0
FEATURE [Part::Cylinder] Cylinder002  label="Cylinder for trim to closed solid"
  Angle = 360
  AttacherType = Attacher::AttachEngine3D
  FirstAngle = 0
  Height = 8
  Placement = pos=(0,0,0) rot=(1,0,0;1.5708rad)
  Radius = 57.5
  SecondAngle = 0
  expr: Height = Spreadsheet.pinion_tooth_heigth
  expr: Radius = Spreadsheet.pinion_circumference / 2
FEATURE [Part::FeaturePython] Slice001  # WARN: FeaturePython — macro-defined, semantics opaque (R4)
  Base = -> Cylinder002
  Mode = 1
  Tolerance = 0
  Tools = -> [Connect013]
FEATURE [Part::FeaturePython] Slice001_child0  label="Slice001.0"  # WARN: FeaturePython — macro-defined, semantics opaque (R4)
  Base = -> Slice001
  FilterType = 1
  Invert = false
  OverrideMaxVal = 0
  WindowFrom = 80
  WindowTo = 100
  items = 0
FEATURE [Part::FeaturePython] Slice001_child1  label="Slice001.1"  # WARN: FeaturePython — macro-defined, semantics opaque (R4)
  Base = -> Slice001
  FilterType = 1
  Invert = false
  OverrideMaxVal = 0
  WindowFrom = 80
  WindowTo = 100
  items = 1
FEATURE [App::DocumentObjectGroup] GrExplode_Slice001  label="Exploded Slice for closing all inner skins"
  Group = -> [Slice001_child0,Slice001_child1]
FEATURE [Part::FeaturePython] Array015  label="Array of pinion teeth"  # Draft array (typed FeaturePython)
  Angle = 360
  ArrayType = 1
  Axis = (0,1,0)
  Base = -> Fillet002
  Center = (0,0,0)
  Fuse = false
  IntervalAxis = (0,0,0)
  IntervalX = (1,0,0)
  IntervalY = (0,1,0)
  IntervalZ = (0,0,1)
  NumberPolar = 20
  NumberX = 1
  NumberY = 1
  NumberZ = 1
  Placement = pos=(0,0,0) rot=(0,1,0;0.15708rad)
  expr: .Placement.Rotation.Angle = 180 / Spreadsheet.pinion_tooth_count
  expr: NumberPolar = Spreadsheet.pinion_tooth_count
FEATURE [Part::FeaturePython] Clone005  label="Closed inner skins"  # Draft clone (typed FeaturePython)
  AttacherType = Attacher::AttachEngine3D
  Fuse = false
  Objects = -> [Slice001_child1]
  Scale = (1,1,1)
FEATURE [Part::MultiFuse] Fusion  label="Fusion of pinion teeth and inner skins"
  Refine = true
  Shapes = -> [Array015,Clone005]
FEATURE [Part::Cylinder] Cylinder003  label="Cylinder for motor shaft hole"
  Angle = 360
  AttacherType = Attacher::AttachEngine3D
  FirstAngle = 0
  Height = 25
  Placement = pos=(0,17,0) rot=(1,0,0;1.5708rad)
  Radius = 3.6
  SecondAngle = 0
  expr: .Placement.Base.y = Spreadsheet.pinion_stock_thick - Spreadsheet.pinion_tooth_heigth
  expr: Height = Spreadsheet.pinion_stock_thick
  expr: Radius = Spreadsheet.pinion_motor_shaft_diameter / 2
FEATURE [Part::Cut] Cut004  label="Pinion with motor shaft cut"
  Base = -> Fusion
  Tool = -> Cylinder003
FEATURE [Part::Cylinder] Cylinder004  label="Cylinder"
  Angle = 360
  AttacherType = Attacher::AttachEngine3D
  FirstAngle = 0
  Height = 17
  Placement = pos=(0,0,0) rot=(-1,0,0;1.5708rad)
  Radius = 19.5
  SecondAngle = 0
  expr: Height = Spreadsheet.pinion_stock_thick - Spreadsheet.pinion_tooth_heigth
  expr: Radius = Spreadsheet.pinion_ring_diameter / 2
FEATURE [Part::Cut] Cut005  label="Pinion back ring"
  Base = -> Cylinder004
  Tool = -> Cylinder003
FEATURE [Part::Cylinder] Cylinder005  label="Cylinder001"
  Angle = 360
  AttacherType = Attacher::AttachEngine3D
  FirstAngle = 0
  Height = 46.2
  Placement = pos=(0,8.5,0) rot=(0,1,0;1.5708rad)
  Radius = 2.15
  SecondAngle = 0
  expr: .Placement.Base.y = (Spreadsheet.pinion_stock_thick - Spreadsheet.pinion_tooth_heigth) / 2
  expr: Height = Spreadsheet.pinion_motor_shaft_diameter + Spreadsheet.pinion_ring_diameter
  expr: Radius = Spreadsheet.pinion_set_screw_hole_diameter / 2
FEATURE [Part::FeaturePython] Array016  # Draft array (typed FeaturePython)
  Angle = 360
  ArrayType = 1
  Axis = (0,1,0)
  Base = -> Cylinder005
  Center = (0,0,0)
  Fuse = false
  IntervalAxis = (0,0,0)
  IntervalX = (1,0,0)
  IntervalY = (0,1,0)
  IntervalZ = (0,0,1)
  NumberPolar = 3
  NumberX = 1
  NumberY = 1
  NumberZ = 1
  expr: NumberPolar = Spreadsheet.pinion_set_screw_count
FEATURE [Part::Cut] Cut006  label="Pinion back ring with set scew holes"
  Base = -> Cut005
  Tool = -> Array016
FEATURE [App::DocumentObjectGroup] Group  label="Leftover building blocks"
  Group = -> [GrExplode_Slice001,GrExplode_Slice,Body006,Common,Body005,Cut002,Cut001,Body,Part__Feature,Body001,Cut006]
FEATURE [Part::FeaturePython] Clone008  label="Pinion - position check"  # Draft clone (typed FeaturePython)
  AttacherType = Attacher::AttachEngine3D
  Fuse = false
  Objects = -> [Cut004]
  Placement = pos=(48.875,0,0) rot=(0,1,0;0.15708rad)
  Scale = (1,1,1)
  expr: .Placement.Base.x = (round(Spreadsheet.pinion_tooth_count / 2) - 1.5) * Spreadsheet.pinion_circumference / Spreadsheet.pinion_tooth_count
  expr: .Placement.Rotation.Angle = 180 / Spreadsheet.pinion_tooth_count
FEATURE [Part::FeaturePython] involutegear  # WARN: FeaturePython — macro-defined, semantics opaque (R4)
  AttacherType = Attacher::AttachEngine3D
  Placement = pos=(0,0,0) rot=(1,0,0;1.5708rad)
  backlash = 0
  beta = 0
  clearance = 0.35
  da = 42.8
  df = 34.6
  double_helix = false
  dw = 40
  head = -0.3
  height = 5
  module = 2
  numpoints = 6
  pressure_angle = 20
  properties_from_tool = false
  reversed_backlash = false
  shift = 0
  simple = false
  teeth = 20
  transverse_pitch = 6.28319
  undercut = false
  version = 0.0.3
FEATURE [Part::FeaturePython] involuterack  # WARN: FeaturePython — macro-defined, semantics opaque (R4)
  AttacherType = Attacher::AttachEngine3D
  Placement = pos=(15.708,0,-20) rot=(0.57735,-0.57735,0.57735;2.0944rad)
  add_endings = true
  beta = 0
  clearance = 0.05
  double_helix = false
  head = 0.2
  height = 5
  module = 2
  pressure_angle = 20
  properties_from_tool = false
  simplified = false
  teeth = 15
  thickness = 5
  transverse_pitch = 6.28319
  version = 0.0.3
  expr: .Placement.Base.x = involutegear.transverse_pitch * 2.5
FEATURE [Sketcher::SketchObject] Sketch003
  FullyConstrained = false
  Placement = pos=(0,0,0) rot=(1,0,0;1.5708rad)
  sketch-geometry (2):
    g0: Circle CenterX=2.6842 CenterY=-18.0679 CenterZ=0 NormalX=0 NormalY=0 NormalZ=1 AngleXU=0 Radius=1
    g1: Circle CenterX=-0.125337 CenterY=-21.0928 CenterZ=0 NormalX=0 NormalY=0 NormalZ=1 AngleXU=0 Radius=1
  constraints (2):
    c: Diameter(g1) = 2
    c: Diameter(g0) = 2
FEATURE [PartDesign::FeatureBase] BaseFeature003
  BaseFeature = -> Cut006
FEATURE [PartDesign::Body] Body007  label="Pinion ring for chamfering"
  BaseFeature = -> Cut006
  Group = -> [BaseFeature003]
  Origin = -> Origin007
  Tip = -> BaseFeature003
FEATURE [Part::MultiFuse] Fusion001  label="Pinion"
  Refine = true
  Shapes = -> [Cut004,Body007]
FEATURE [PartDesign::FeatureBase] BaseFeature004
  BaseFeature = -> Array
FEATURE [Sketcher::SketchObject] Sketch004
  AttachmentOffset = pos=(0,0,8) rot=(0,0,1;0rad)
  ExternalGeometry = -> [BaseFeature004]
  FullyConstrained = true
  MapMode = 5
  Placement = pos=(0,-8,-1.8e-15) rot=(1,0,0;1.5708rad)
  Support = -> [XZ_Plane008]
  expr: .AttachmentOffset.Base.z = Spreadsheet.pinion_tooth_heigth
  sketch-geometry (4):
    g0: LineSegment StartX=-2.875 StartY=-21.65 StartZ=0 EndX=204.125 EndY=-21.65 EndZ=0
    g1: LineSegment StartX=204.125 StartY=-21.65 StartZ=0 EndX=204.125 EndY=4.35 EndZ=0
    g2: LineSegment StartX=204.125 StartY=4.35 StartZ=0 EndX=-2.875 EndY=4.35 EndZ=0
    g3: LineSegment StartX=-2.875 StartY=4.35 StartZ=0 EndX=-2.875 EndY=-21.65 EndZ=0
  constraints (10):
    c: Coincident(g0,g1)
    c: Coincident(g1,g2)
    c: Coincident(g2,g3)
    c: Coincident(g3,g0)
    c: Horizontal(g2)
    c: Vertical(g1)
    c: Vertical(g3)
    c: Distance(g1) = 26
    c: Coincident(g0,g-5)
    c: Coincident(g-4,g0)
FEATURE [PartDesign::Pad] Pad001
  BaseFeature = -> BaseFeature004
  Direction = (1,1,1)
  Length = 3.6
  Length2 = 100
  Profile = -> Sketch004
  Refine = true
  Type = 0
  expr: Length = 11.6 - Spreadsheet.pinion_tooth_heigth
FEATURE [Sketcher::SketchObject] Sketch005
  FullyConstrained = false
  MapMode = 5
  Placement = pos=(0,0,0) rot=(1,0,0;1.5708rad)
  Support = -> [XZ_Plane008]
  expr: Constraints[1] = 15 - Spreadsheet.rack_tooth_spacing / 2
  sketch-geometry (1):
    g0: Circle CenterX=12.125 CenterY=-10.5 CenterZ=0 NormalX=0 NormalY=0 NormalZ=1 AngleXU=0 Radius=4.11992
  constraints (2):
    c: DistanceY(g-1,g0) = -10.5
    c: DistanceX(g-2,g0) = 12.125
FEATURE [PartDesign::Hole] Hole
  BaseFeature = -> Pad001
  CustomThreadClearance = 0
  Depth = 25
  DepthType = 1
  Diameter = 5.3
  DrillForDepth = false
  DrillPoint = 1
  DrillPointAngle = 118
  HoleCutCountersinkAngle = 90
  HoleCutCustomValues = false
  HoleCutDepth = 5.5
  HoleCutDiameter = 9.7
  HoleCutType = 1
  ModelThread = false
  Profile = -> Sketch005
  Reversed = true
  Tapered = false
  TaperedAngle = 90
  ThreadClass = 0
  ThreadDepth = 23.5
  ThreadDepthType = 0
  ThreadDirection = 0
  ThreadFit = 0
  ThreadSize = 0
  ThreadType = 0
  Threaded = false
  UseCustomThreadClearance = false
FEATURE [PartDesign::LinearPattern] LinearPattern
  BaseFeature = -> Hole
  Direction = -> Sketch005 [H_Axis]
  Length = 180
  Occurrences = 4
  Originals = -> [Hole]
  expr: Length = (Occurrences - 1) * 60
FEATURE [PartDesign::Body] Body008  label="Rack with web and material thickness"
  BaseFeature = -> Array
  Group = -> [BaseFeature004,Sketch004,Pad001,Sketch005,Hole,LinearPattern]
  Origin = -> Origin008
  Placement = pos=(-5.75,0,-18.3028) rot=(0,0,1;0rad)
  Tip = -> LinearPattern
  expr: .Placement.Base.x = Spreadsheet.rack_tooth_spacing * -1
  expr: .Placement.Base.z = Spreadsheet.pinion_circumference / pi / -2
FEATURE [Part::FeaturePython] Array017  label="Rack - position fixed"  # Draft array (typed FeaturePython)
  AlwaysSyncPlacement = false
  Angle = 360
  ArrayType = 0
  Axis = (0,0,1)
  Base = -> Body008
  Center = (0,0,0)
  Count = 1
  ExpandArray = false
  Fuse = false
  IntervalAxis = (0,0,0)
  IntervalX = (100,0,0)
  IntervalY = (0,100,0)
  IntervalZ = (0,0,100)
  NumberCircles = 3
  NumberPolar = 5
  NumberX = 1
  NumberY = 1
  NumberZ = 1
  PlacementList = 1 placements: [(-5.75,0,-18.3028)]
  RadialDistance = 50
  ScaleList = (1) [(1,1,1)]
  Symmetry = 1
  TangentialDistance = 25
COMPONENT P7 — same part as P6; its construction recipe is shown at P6.
COMPONENT P8 — geometry summary ("Nested parts"; no construction recipe available for this part):
  bounding box: 2434.8 x 1225.8 x 11.6 mm
  tessellated surface: 484 triangles
  volume: 13220874 mm^3 (38% of its bounding box)
  symmetry: mirror-symmetric across its z mid-plane
COMPONENT P9 — recipe-attached ("Wood sheets", modeled in this document).
Construction recipe (the document's own serialized feature program — sketch geometry with constraints, then the solid features built on it; lengths are millimeters unless a unit is written):

FEATURE [Sketcher::SketchObject] Sketch003
  FullyConstrained = true
  MapMode = 5
  Support = -> [XY_Plane001]
  expr: Constraints[8] = dd.ddBed_size_X
  expr: Constraints[9] = dd.ddBed_size_Y
  sketch-geometry (4):
    g0: LineSegment StartX=-610 StartY=-1220 StartZ=0 EndX=610 EndY=-1220 EndZ=0
    g1: LineSegment StartX=610 StartY=-1220 StartZ=0 EndX=610 EndY=1220 EndZ=0
    g2: LineSegment StartX=610 StartY=1220 StartZ=0 EndX=-610 EndY=1220 EndZ=0
    g3: LineSegment StartX=-610 StartY=1220 StartZ=0 EndX=-610 EndY=-1220 EndZ=0
  constraints (10):
    c: Coincident(g0,g1)
    c: Coincident(g1,g2)
    c: Coincident(g2,g3)
    c: Coincident(g3,g0)
    c: Horizontal(g0)
    c: Vertical(g1)
    c: Symmetric(g1,g2,g-2)
    c: Symmetric(g2,g0,g-1)
    c: Distance(g0) = 1220
    c: Distance(g1) = 2440
FEATURE [PartDesign::Pad] Pad003
  Direction = (0,0,1)
  Length = 19
  Length2 = 10
  Profile = -> Sketch003
  ReferenceAxis = -> Sketch003 [N_Axis]
  Reversed = true
  Type = 0
  expr: Length = dd.ddMDF_thickness
FEATURE [PartDesign::Body] Body001  label="MDF sacrafcial layer"
  Group = -> [Sketch003,Pad003]
  Origin = -> Origin001
  Tip = -> Pad003
FEATURE [Sketcher::SketchObject] Sketch004
  FullyConstrained = true
  MapMode = 5
  Support = -> [XY_Plane002]
  expr: Constraints[8] = dd.ddBed_size_X
  expr: Constraints[9] = dd.ddBed_size_Y
  sketch-geometry (4):
    g0: LineSegment StartX=-610 StartY=-1220 StartZ=0 EndX=610 EndY=-1220 EndZ=0
    g1: LineSegment StartX=610 StartY=-1220 StartZ=0 EndX=610 EndY=1220 EndZ=0
    g2: LineSegment StartX=610 StartY=1220 StartZ=0 EndX=-610 EndY=1220 EndZ=0
    g3: LineSegment StartX=-610 StartY=1220 StartZ=0 EndX=-610 EndY=-1220 EndZ=0
  constraints (10):
    c: Coincident(g0,g1)
    c: Coincident(g1,g2)
    c: Coincident(g2,g3)
    c: Coincident(g3,g0)
    c: Horizontal(g0)
    c: Vertical(g1)
    c: Symmetric(g1,g2,g-2)
    c: Symmetric(g2,g0,g-1)
    c: Distance(g0) = 1220
    c: Distance(g1) = 2440
FEATURE [PartDesign::Pad] Pad004
  Direction = (0,0,1)
  Length = 18
  Length2 = 10
  Profile = -> Sketch004
  ReferenceAxis = -> Sketch004 [N_Axis]
  Reversed = true
  Type = 0
  expr: Length = dd.ddPlywood_thickness
FEATURE [PartDesign::Body] Body002  label="Plywood top"
  Group = -> [Sketch004,Pad004]
  Origin = -> Origin002
  Placement = pos=(0,0,-19) rot=(0,0,1;0rad)
  Tip = -> Pad004
  expr: .Placement.Base.z = -dd.ddMDF_thickness
FEATURE [Sketcher::SketchObject] Sketch005
  FullyConstrained = true
  MapMode = 5
  Support = -> [XY_Plane003]
  expr: Constraints[8] = dd.ddBed_size_X
  expr: Constraints[9] = dd.ddBed_size_Y
  sketch-geometry (4):
    g0: LineSegment StartX=-610 StartY=-1220 StartZ=0 EndX=610 EndY=-1220 EndZ=0
    g1: LineSegment StartX=610 StartY=-1220 StartZ=0 EndX=610 EndY=1220 EndZ=0
    g2: LineSegment StartX=610 StartY=1220 StartZ=0 EndX=-610 EndY=1220 EndZ=0
    g3: LineSegment StartX=-610 StartY=1220 StartZ=0 EndX=-610 EndY=-1220 EndZ=0
  constraints (10):
    c: Coincident(g0,g1)
    c: Coincident(g1,g2)
    c: Coincident(g2,g3)
    c: Coincident(g3,g0)
    c: Horizontal(g0)
    c: Vertical(g1)
    c: Symmetric(g1,g2,g-2)
    c: Symmetric(g2,g0,g-1)
    c: Distance(g0) = 1220
    c: Distance(g1) = 2440
FEATURE [PartDesign::Pad] Pad005
  Direction = (0,0,1)
  Length = 18
  Length2 = 10
  Profile = -> Sketch005
  ReferenceAxis = -> Sketch005 [N_Axis]
  Reversed = true
  Type = 0
  expr: Length = dd.ddPlywood_thickness
FEATURE [PartDesign::Body] Body003  label="Plywood bottom"
  Group = -> [Sketch005,Pad005]
  Origin = -> Origin003
  Placement = pos=(0,0,-103) rot=(0,0,1;0rad)
  Tip = -> Pad005
  expr: .Placement.Base.z = -dd.ddMDF_thickness - dd.ddCore_heigth - dd.ddPlywood_thickness
COMPONENT P10 — recipe-attached ("Gantry", modeled in this document).
Construction recipe (the document's own serialized feature program — sketch geometry with constraints, then the solid features built on it; lengths are millimeters unless a unit is written):

FEATURE [Sketcher::SketchObject] Sketch009
  FullyConstrained = true
  MapMode = 5
  Placement = pos=(0,0,0) rot=(1,0,0;1.5708rad)
  Support = -> [XZ_Plane006]
  expr: Constraints[8] = dd.ddX_rail_length + 20
  expr: Constraints[9] = dd.ddGantry_heigth - (dd.ddPhenolic_thickness - dd.ddAlignment_pocket_depth) * 2
  sketch-geometry (4):
    g0: LineSegment StartX=-750 StartY=122.8 StartZ=0 EndX=750 EndY=122.8 EndZ=0
    g1: LineSegment StartX=750 StartY=122.8 StartZ=0 EndX=750 EndY=0 EndZ=0
    g2: LineSegment StartX=750 StartY=0 StartZ=0 EndX=-750 EndY=0 EndZ=0
    g3: LineSegment StartX=-750 StartY=0 StartZ=0 EndX=-750 EndY=122.8 EndZ=0
  constraints (11):
    c: Coincident(g0,g1)
    c: Coincident(g1,g2)
    c: Coincident(g2,g3)
    c: Coincident(g3,g0)
    c: Horizontal(g2)
    c: Vertical(g1)
    c: Vertical(g3)
    c: Symmetric(g0,g0,g-2)
    c: Distance(g0) = 1500
    c: Distance(g3) = 122.8
    c: PointOnObject(g2,g-1)
FEATURE [PartDesign::Pad] Pad008
  Direction = (0,-1,-2e-16)
  Length = 11.6
  Length2 = 10
  Placement = pos=(0,0,0) rot=(1,0,0;1.5708rad)
  Profile = -> Sketch009
  ReferenceAxis = -> Sketch009 [N_Axis]
  Reversed = true
  Type = 0
  expr: Length = dd.ddPhenolic_thickness
FEATURE [PartDesign::Body] Body006  label="Gantry front plate"
  Group = -> [Sketch009,Pad008]
  Origin = -> Origin006
  Placement = pos=(0,0,68.6) rot=(0,0,1;0rad)
  Tip = -> Pad008
  expr: .Placement.Base.z = dd.ddGantry_to_bed_clearance + dd.ddPhenolic_thickness - dd.ddAlignment_pocket_depth
FEATURE [Sketcher::SketchObject] Sketch010
  FullyConstrained = true
  MapMode = 5
  Placement = pos=(0,0,0) rot=(0.57735,0.57735,0.57735;2.0944rad)
  Support = -> [YZ_Plane007]
  expr: Constraints[10] = -dd.ddPhenolic_thickness
  expr: Constraints[11] = -dd.ddPhenolic_thickness + dd.ddAlignment_pocket_depth
  expr: Constraints[12] = -dd.ddRail_alignment_stickout
  expr: Constraints[13] = dd.ddPhenolic_thickness
  expr: Constraints[14] = dd.ddGantry_depth
  expr: Constraints[23] = dd.ddGantry_depth - dd.ddPhenolic_thickness
  sketch-geometry (8):
    g0: LineSegment StartX=-2 StartY=0 StartZ=0 EndX=62 EndY=0 EndZ=0
    g1: LineSegment StartX=50.4 StartY=-11.6 StartZ=0 EndX=11.6 EndY=-11.6 EndZ=0
    g2: LineSegment StartX=11.6 StartY=-11.6 StartZ=0 EndX=11.6 EndY=-3.6 EndZ=0
    g3: LineSegment StartX=11.6 StartY=-3.6 StartZ=0 EndX=-2 EndY=-3.6 EndZ=0
    g4: LineSegment StartX=-2 StartY=-3.6 StartZ=0 EndX=-2 EndY=0 EndZ=0
    g5: LineSegment StartX=50.4 StartY=-11.6 StartZ=0 EndX=50.4 EndY=-3.6 EndZ=0
    g6: LineSegment StartX=50.4 StartY=-3.6 StartZ=0 EndX=62 EndY=-3.6 EndZ=0
    g7: LineSegment StartX=62 StartY=-3.6 StartZ=0 EndX=62 EndY=0 EndZ=0
  constraints (24):
    c: PointOnObject(g0,g-1)
    c: Horizontal(g0)
    c: Horizontal(g1)
    c: Coincident(g1,g2)
    c: Coincident(g2,g3)
    c: Horizontal(g3)
    c: Coincident(g3,g4)
    c: Coincident(g4,g0)
    c: Vertical(g4)
    c: Vertical(g2)
    c: DistanceY(g-1,g1) = -11.6
    c: DistanceY(g-1,g3) = -3.6
    c: DistanceX(g-2,g0) = -2
    c: DistanceX(g-2,g2) = 11.6
    c: DistanceX(g-2,g0) = 62
    c: Coincident(g1,g5)
    c: Vertical(g5)
    c: Coincident(g5,g6)
    c: Coincident(g6,g7)
    c: Coincident(g7,g0)
    c: Vertical(g7)
    c: Horizontal(g6)
    c: Horizontal(g5,g2)
    c: DistanceX(g-2,g5) = 50.4
FEATURE [PartDesign::Pad] Pad009
  Direction = (1,-2e-16,3e-16)
  Length = 1500
  Length2 = 10
  Midplane = true
  Placement = pos=(0,0,0) rot=(0.57735,0.57735,0.57735;2.0944rad)
  Profile = -> Sketch010
  ReferenceAxis = -> Sketch010 [N_Axis]
  Type = 0
  expr: Length = dd.ddX_rail_length + 20
FEATURE [PartDesign::Body] Body007  label="Gantry top plate"
  Group = -> [Sketch010,Pad009]
  Origin = -> Origin007
  Placement = pos=(0,0,195) rot=(0,0,1;0rad)
  Tip = -> Pad009
  expr: .Placement.Base.z = dd.ddGantry_to_bed_clearance + dd.ddGantry_heigth
FEATURE [Sketcher::SketchObject] Sketch014
  FullyConstrained = true
  MapMode = 5
  Placement = pos=(0,0,0) rot=(1,0,0;1.5708rad)
  Support = -> [XZ_Plane013]
  expr: Constraints[8] = dd.ddX_rail_length + 20
  expr: Constraints[9] = dd.ddGantry_heigth - (dd.ddPhenolic_thickness - dd.ddAlignment_pocket_depth) * 2
  sketch-geometry (4):
    g0: LineSegment StartX=-750 StartY=122.8 StartZ=0 EndX=750 EndY=122.8 EndZ=0
    g1: LineSegment StartX=750 StartY=122.8 StartZ=0 EndX=750 EndY=0 EndZ=0
    g2: LineSegment StartX=750 StartY=0 StartZ=0 EndX=-750 EndY=0 EndZ=0
    g3: LineSegment StartX=-750 StartY=0 StartZ=0 EndX=-750 EndY=122.8 EndZ=0
  constraints (11):
    c: Coincident(g0,g1)
    c: Coincident(g1,g2)
    c: Coincident(g2,g3)
    c: Coincident(g3,g0)
    c: Horizontal(g2)
    c: Vertical(g1)
    c: Vertical(g3)
    c: Symmetric(g0,g0,g-2)
    c: Distance(g0) = 1500
    c: Distance(g3) = 122.8
    c: PointOnObject(g2,g-1)
FEATURE [PartDesign::Pad] Pad013
  Direction = (0,-1,-2e-16)
  Length = 11.6
  Length2 = 10
  Placement = pos=(0,0,0) rot=(1,0,0;1.5708rad)
  Profile = -> Sketch014
  ReferenceAxis = -> Sketch014 [N_Axis]
  Reversed = true
  Type = 0
  expr: Length = dd.ddPhenolic_thickness
FEATURE [PartDesign::Body] Body011  label="Gantry back plate"
  Group = -> [Sketch014,Pad013]
  Origin = -> Origin013
  Placement = pos=(0,50.4,68.6) rot=(0,0,1;0rad)
  Tip = -> Pad013
  expr: .Placement.Base.y = dd.ddGantry_depth - dd.ddPhenolic_thickness
  expr: .Placement.Base.z = dd.ddGantry_to_bed_clearance + dd.ddPhenolic_thickness - dd.ddAlignment_pocket_depth
FEATURE [Sketcher::SketchObject] Sketch015
  FullyConstrained = true
  MapMode = 5
  Placement = pos=(0,0,0) rot=(0.57735,0.57735,0.57735;2.0944rad)
  Support = -> [YZ_Plane014]
  expr: Constraints[10] = -dd.ddGantry_heigth + dd.ddPhenolic_thickness - dd.ddAlignment_pocket_depth
  expr: Constraints[11] = -dd.ddRail_alignment_stickout
  expr: Constraints[12] = dd.ddPhenolic_thickness
  expr: Constraints[13] = dd.ddGantry_depth
  expr: Constraints[22] = dd.ddGantry_depth - dd.ddPhenolic_thickness
  expr: Constraints[23] = -dd.ddGantry_heigth
  expr: Constraints[9] = -dd.ddGantry_heigth + dd.ddPhenolic_thickness
  sketch-geometry (8):
    g0: LineSegment StartX=-2 StartY=-130 StartZ=0 EndX=62 EndY=-130 EndZ=0
    g1: LineSegment StartX=50.4 StartY=-118.4 StartZ=0 EndX=11.6 EndY=-118.4 EndZ=0
    g2: LineSegment StartX=11.6 StartY=-118.4 StartZ=0 EndX=11.6 EndY=-126.4 EndZ=0
    g3: LineSegment StartX=11.6 StartY=-126.4 StartZ=0 EndX=-2 EndY=-126.4 EndZ=0
    g4: LineSegment StartX=-2 StartY=-126.4 StartZ=0 EndX=-2 EndY=-130 EndZ=0
    g5: LineSegment StartX=50.4 StartY=-118.4 StartZ=0 EndX=50.4 EndY=-126.4 EndZ=0
    g6: LineSegment StartX=50.4 StartY=-126.4 StartZ=0 EndX=62 EndY=-126.4 EndZ=0
    g7: LineSegment StartX=62 StartY=-126.4 StartZ=0 EndX=62 EndY=-130 EndZ=0
  constraints (24):
    c: Horizontal(g0)
    c: Horizontal(g1)
    c: Coincident(g1,g2)
    c: Coincident(g2,g3)
    c: Horizontal(g3)
    c: Coincident(g3,g4)
    c: Coincident(g4,g0)
    c: Vertical(g4)
    c: Vertical(g2)
    c: DistanceY(g-1,g1) = -118.4
    c: DistanceY(g-1,g3) = -126.4
    c: DistanceX(g-2,g0) = -2
    c: DistanceX(g-2,g2) = 11.6
    c: DistanceX(g-2,g0) = 62
    c: Coincident(g1,g5)
    c: Vertical(g5)
    c: Coincident(g5,g6)
    c: Coincident(g6,g7)
    c: Coincident(g7,g0)
    c: Vertical(g7)
    c: Horizontal(g6)
    c: Horizontal(g5,g2)
    c: DistanceX(g-2,g5) = 50.4
    c: DistanceY(g-1,g0) = -130
FEATURE [PartDesign::Pad] Pad014
  Direction = (1,-2e-16,3e-16)
  Length = 1500
  Length2 = 10
  Midplane = true
  Placement = pos=(0,0,0) rot=(0.57735,0.57735,0.57735;2.0944rad)
  Profile = -> Sketch015
  ReferenceAxis = -> Sketch015 [N_Axis]
  Type = 0
  expr: Length = dd.ddX_rail_length + 20
FEATURE [PartDesign::Body] Body012  label="Gantry bottom plate"
  Group = -> [Sketch015,Pad014]
  Origin = -> Origin014
  Placement = pos=(0,0,195) rot=(0,0,1;0rad)
  Tip = -> Pad014
  expr: .Placement.Base.z = dd.ddGantry_to_bed_clearance + dd.ddGantry_heigth
FEATURE [Sketcher::SketchObject] Sketch016
  FullyConstrained = true
  MapMode = 5
  Placement = pos=(0,0,0) rot=(0.57735,0.57735,0.57735;2.0944rad)
  Support = -> [YZ_Plane015]
  expr: Constraints[10] = dd.ddPhenolic_thickness
  expr: Constraints[11] = dd.ddGantry_depth - dd.ddPhenolic_thickness
  expr: Constraints[8] = -dd.ddGantry_heigth / 2 + dd.ddPhenolic_thickness / 2
  expr: Constraints[9] = -dd.ddGantry_heigth / 2 - dd.ddPhenolic_thickness / 2
  sketch-geometry (4):
    g0: LineSegment StartX=11.6 StartY=-59.2 StartZ=0 EndX=50.4 EndY=-59.2 EndZ=0
    g1: LineSegment StartX=50.4 StartY=-59.2 StartZ=0 EndX=50.4 EndY=-70.8 EndZ=0
    g2: LineSegment StartX=50.4 StartY=-70.8 StartZ=0 EndX=11.6 EndY=-70.8 EndZ=0
    g3: LineSegment StartX=11.6 StartY=-70.8 StartZ=0 EndX=11.6 EndY=-59.2 EndZ=0
  constraints (12):
    c: Coincident(g0,g1)
    c: Coincident(g1,g2)
    c: Coincident(g2,g3)
    c: Coincident(g3,g0)
    c: Horizontal(g0)
    c: Horizontal(g2)
    c: Vertical(g1)
    c: Vertical(g3)
    c: DistanceY(g-1,g0) = -59.2
    c: DistanceY(g-1,g1) = -70.8
    c: DistanceX(g-2,g0) = 11.6
    c: DistanceX(g-2,g0) = 50.4
FEATURE [PartDesign::Pad] Pad015
  Direction = (1,-2e-16,3e-16)
  Length = 1500
  Length2 = 10
  Midplane = true
  Placement = pos=(0,0,0) rot=(0.57735,0.57735,0.57735;2.0944rad)
  Profile = -> Sketch016
  ReferenceAxis = -> Sketch016 [N_Axis]
  Type = 0
  expr: Length = dd.ddX_rail_length + 20
FEATURE [PartDesign::Body] Body013  label="Gantry mid plate"
  Group = -> [Sketch016,Pad015]
  Origin = -> Origin015
  Placement = pos=(0,0,195) rot=(0,0,1;0rad)
  Tip = -> Pad015
  expr: .Placement.Base.z = dd.ddGantry_to_bed_clearance + dd.ddGantry_heigth
FEATURE [Sketcher::SketchObject] Sketch017
  FullyConstrained = false
  MapMode = 5
  Placement = pos=(0,0,0) rot=(0.57735,0.57735,0.57735;2.0944rad)
  Support = -> [YZ_Plane016]
  expr: Constraints[21] = <<Rail Y>>.Placement.Base[2] + dd.ddBearing_block_width / 2
  expr: Constraints[22] = <<Spindle>>.Placement.Base[1] + dd.ddY_block_to_spindle_offset
  expr: Constraints[23] = <<Spindle>>.Placement.Base[1] + dd.ddY_block_to_spindle_offset + dd.ddY_block_spacing + dd.ddBearing_block_length
  sketch-geometry (11):
    g0: LineSegment StartX=9.08412 StartY=180.306 StartZ=0 EndX=9.08412 EndY=64.4413 EndZ=0
    g1: LineSegment StartX=-63.4784 StartY=-27.5 StartZ=0 EndX=-109.55 EndY=-27.5 EndZ=0
    g2: LineSegment StartX=-109.55 StartY=-27.5 StartZ=0 EndX=-109.55 EndY=-104.165 EndZ=0
    g3: LineSegment StartX=-109.55 StartY=-104.165 StartZ=0 EndX=31.85 EndY=-104.165 EndZ=0
    g4: LineSegment StartX=49.3808 StartY=64.4413 StartZ=0 EndX=49.3808 EndY=180.306 EndZ=0
    g5: LineSegment StartX=49.3808 StartY=180.306 StartZ=0 EndX=9.08412 EndY=180.306 EndZ=0
    g6: LineSegment StartX=-63.4784 StartY=-27.5 StartZ=0 EndX=1.57454 EndY=64.4413 EndZ=0
    g7: LineSegment StartX=1.57454 StartY=64.4413 StartZ=0 EndX=9.08412 EndY=64.4413 EndZ=0
    g8: LineSegment StartX=49.3808 StartY=64.4413 StartZ=0 EndX=58.9127 EndY=64.4413 EndZ=0
    g9: LineSegment StartX=31.85 StartY=-104.165 StartZ=0 EndX=31.85 EndY=-27.5 EndZ=0
    g10: LineSegment StartX=31.85 StartY=-27.5 StartZ=0 EndX=58.9127 EndY=64.4413 EndZ=0
  constraints (25):
    c: Vertical(g0)
    c: Horizontal(g1)
    c: Coincident(g1,g2)
    c: Vertical(g2)
    c: Coincident(g2,g3)
    c: Horizontal(g3)
    c: Vertical(g4)
    c: Coincident(g4,g5)
    c: Coincident(g5,g0)
    c: Horizontal(g5)
    c: Horizontal(g4,g0)
    c: Coincident(g1,g6)
    c: Coincident(g6,g7)
    c: Coincident(g7,g0)
    c: Coincident(g4,g8)
    c: Horizontal(g7)
    c: Horizontal(g8)
    c: Coincident(g3,g9)
    c: Vertical(g9)
    c: Coincident(g9,g10)
    c: Coincident(g10,g8)
    c: DistanceY(g-1,g1) = -27.5
    c: DistanceX(g-2,g1) = -109.55
    c: DistanceX(g-2,g9) = 31.85
    c: Horizontal(g9,g1)
FEATURE [PartDesign::Pad] Pad016
  Direction = (1,-2e-16,3e-16)
  Length = 11.6
  Length2 = 10
  Placement = pos=(0,0,0) rot=(0.57735,0.57735,0.57735;2.0944rad)
  Profile = -> Sketch017
  ReferenceAxis = -> Sketch017 [N_Axis]
  Type = 0
  expr: Length = dd.ddPhenolic_thickness
FEATURE [PartDesign::Body] Body014  label="Gantry foot wall"
  Group = -> [Sketch017,Pad016]
  Origin = -> Origin016
  Placement = pos=(640,0,0) rot=(0,0,1;0rad)
  Tip = -> Pad016
  expr: .Placement.Base.x = <<Rail Y>>.Placement.Base[0] + dd.ddBearing_block_heigth
FEATURE [Sketcher::SketchObject] Sketch021
  FullyConstrained = true
  MapMode = 5
  Placement = pos=(0,0,0) rot=(0.57735,0.57735,0.57735;2.0944rad)
  Support = -> [YZ_Plane019]
  expr: Constraints[10] = dd.ddRail_width
  expr: Constraints[11] = -dd.ddRail_heigth
  sketch-geometry (5):
    g0: LineSegment StartX=0 StartY=0 StartZ=0 EndX=0 EndY=15 EndZ=0
    g1: LineSegment StartX=0 StartY=15 StartZ=0 EndX=-13 EndY=15 EndZ=0
    g2: LineSegment StartX=-13 StartY=15 StartZ=0 EndX=-13 EndY=0 EndZ=0
    g3: LineSegment StartX=-13 StartY=0 StartZ=0 EndX=0 EndY=0 EndZ=0
    g4: GeomPoint X=-6.5 Y=7.5 Z=0
  constraints (12):
    c: Coincident(g0,g1)
    c: Coincident(g1,g2)
    c: Coincident(g2,g3)
    c: Coincident(g3,g0)
    c: Horizontal(g1)
    c: Horizontal(g3)
    c: Vertical(g0)
    c: Vertical(g2)
    c: Symmetric(g1,g0,g4)
    c: Coincident(g0,g-1)
    c: DistanceY(g-1,g1) = 15
    c: DistanceX(g-2,g1) = -13
FEATURE [PartDesign::Pad] Pad018
  Direction = (1,-2e-16,3e-16)
  Length = 1480
  Length2 = 10
  Midplane = true
  Placement = pos=(0,0,0) rot=(0.57735,0.57735,0.57735;2.0944rad)
  Profile = -> Sketch021
  ReferenceAxis = -> Sketch021 [N_Axis]
  Type = 0
  expr: Length = dd.ddX_rail_length
FEATURE [PartDesign::Body] Body016  label="Rail X"
  Group = -> [Sketch021,Pad018]
  Origin = -> Origin019
  Placement = pos=(0,0,68.6) rot=(0,0,1;0rad)
  Tip = -> Pad018
  expr: .Placement.Base.z = dd.ddGantry_to_bed_clearance + dd.ddPhenolic_thickness - dd.ddAlignment_pocket_depth
PROVENANCE & LICENSES
A FreeCAD (.FCStd) document from a public repository crawl; recipes are the document's own serialized feature recipes (and, for linked parts, companion documents' recipes).
License: cc0-1.0.
